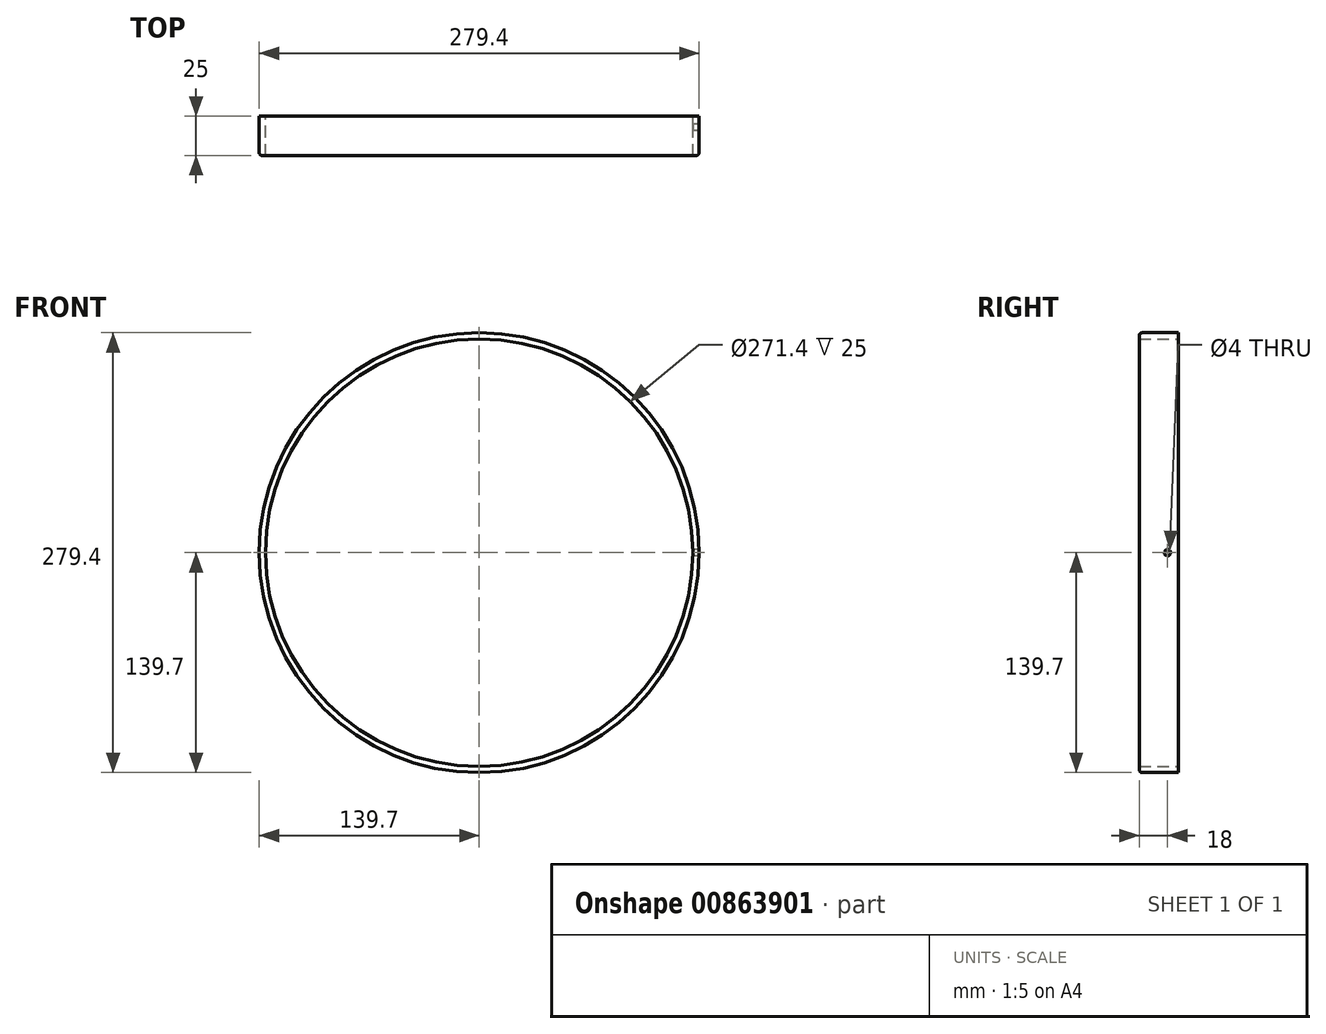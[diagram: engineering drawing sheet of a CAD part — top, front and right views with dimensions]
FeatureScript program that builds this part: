
annotation { "Feature Type Name" : "Feature", "Feature Type Description" : "" }
export const myFeature = defineFeature(function(context is Context, id is Id, definition is map)
    precondition{}
    {
        {
            var Q0;
            Q0=qCreatedBy(makeId("Front.planeOp"),FACE);
            var sketch = newSketch(context, id + "F0", { "sketchPlane" : qUnion([Q0])});
            skCircle(sketch, "E0", {"center": v(0, 0) * mm, "radius": 139.7 * mm});
            skCircle(sketch, "E1", {"center": v(0, 0) * mm, "radius": 135.7 * mm});
            skSolve(sketch);
        }
        {
            var Q0;
            Q0=makeQuery(id+"F0.imprint","IMPRINT",FACE,{"disambiguationData":[TD([[makeQuery(id+"F0.imprint","IMPRINT",EDGE,{"derivedFrom":sQuery(id+"F0.wireOp",EDGE,"E0")}),1.0]])]});
            extrude(context, id + "F1", {"entities" : qUnion([Q0]), "depth" : 25 * mm, "offsetDistance" : 25 * mm});
        }
        {
            var Q0;
            Q0=qCreatedBy(makeId("Right.planeOp"),FACE);
            var sketch = newSketch(context, id + "F2", { "sketchPlane" : qUnion([Q0])});
            skLineSegment(sketch, "E2", {"start": v(0, 0) * mm, "end": v(-19.93, 0) * mm, "construction": true});
            skLineSegment(sketch, "E3", {"start": v(0, 7.8) * mm, "end": v(0, -10.28) * mm, "construction": true});
            skPoint(sketch, "E4", {"position": v(-7, 0) * mm});
            skSolve(sketch);
        }
        {
            var Q0;
            Q0=sQuery(id+"F2.wireOp",VERTEX,"E4");
            var Q1;
            Q1=makeQuery(id+"F1.opExtrude","SWEPT_BODY",BODY,{"disambiguationData":[OSD([sQuery(id+"F0.wireOp",EDGE,"E0"),sQuery(id+"F0.wireOp",EDGE,"E1")])]});
            hole(context, id + "F3", {"style" : HoleStyle.SIMPLE, "endStyle" : HoleEndStyle.THROUGH, "oppositeDirection" : true, "holeDiameter" : 4 * mm, "majorDiameter" : 5 * mm, "isTappedThrough" : true, "tappedDepth" : 12 * mm, "tapClearance" : 3, "locations" : qUnion([Q0]), "scope" : qUnion([Q1])});
        }
        {
            var Q0;
            Q0=makeQuery(id+"F1.opExtrude","CAP_EDGE",EDGE,{"disambiguationData":[OSD([sQuery(id+"F0.wireOp",EDGE,"E0")])],"isStart":false});
            fillet(context, id + "F4", {"entities" : qUnion([Q0]), "radius" : 2 * mm, "tangentPropagation" : true, "allowEdgeOverflow" : false});
        }
    });
